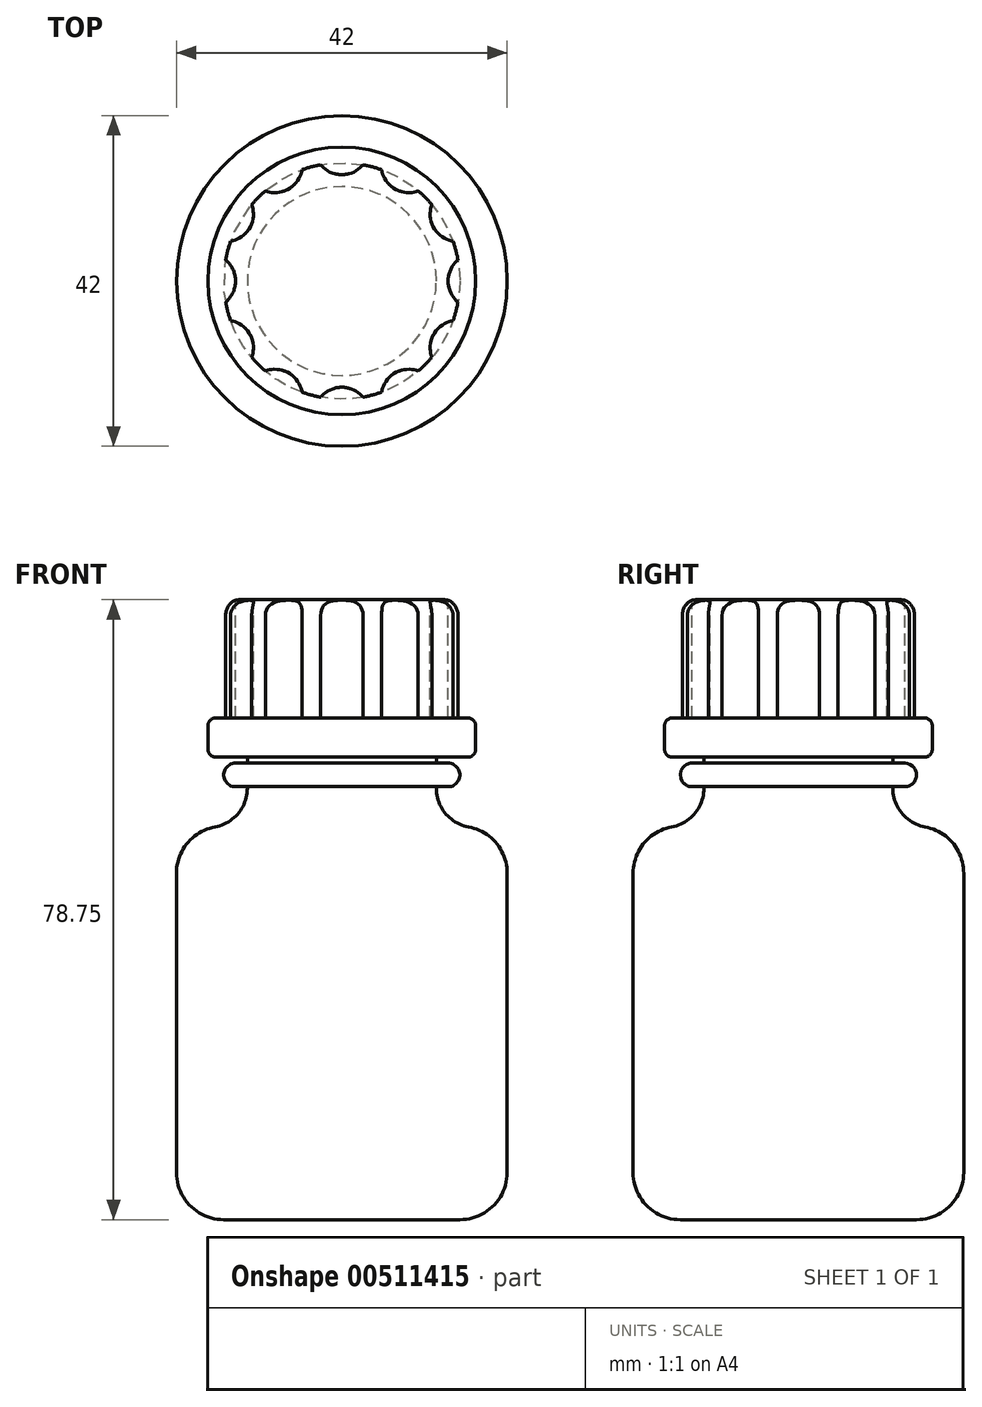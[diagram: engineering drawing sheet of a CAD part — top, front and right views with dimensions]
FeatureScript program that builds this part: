
annotation { "Feature Type Name" : "Feature", "Feature Type Description" : "" }
export const myFeature = defineFeature(function(context is Context, id is Id, definition is map)
    precondition{}
    {
        {
            var Q0;
            Q0=qCreatedBy(makeId("Front.planeOp"),FACE);
            var sketch = newSketch(context, id + "F0", { "sketchPlane" : qUnion([Q0])});
            skLineSegment(sketch, "E0", {"start": v(0, 0) * mm, "end": v(-21, 0) * mm});
            skLineSegment(sketch, "E1", {"start": v(-21, 0) * mm, "end": v(-21, 50) * mm});
            skLineSegment(sketch, "E2", {"start": v(-21, 50) * mm, "end": v(-12, 50) * mm});
            skLineSegment(sketch, "E3", {"start": v(-12, 50) * mm, "end": v(-12, 55) * mm});
            skLineSegment(sketch, "E4", {"start": v(-12, 55) * mm, "end": v(-15, 55) * mm});
            skLineSegment(sketch, "E5", {"start": v(-15, 55) * mm, "end": v(-15, 58) * mm});
            skLineSegment(sketch, "E6", {"start": v(-15, 58) * mm, "end": v(-12, 58) * mm});
            skLineSegment(sketch, "E7", {"start": v(-12, 58) * mm, "end": v(-12, 58.75) * mm});
            skLineSegment(sketch, "E8", {"start": v(-12, 58.75) * mm, "end": v(-17, 58.75) * mm});
            skLineSegment(sketch, "E9", {"start": v(-15, 78.75) * mm, "end": v(0, 78.75) * mm});
            skLineSegment(sketch, "E10", {"start": v(0, 78.75) * mm, "end": v(0, 0) * mm});
            skLineSegment(sketch, "E11", {"start": v(-17, 63.75) * mm, "end": v(-15, 63.75) * mm});
            skLineSegment(sketch, "E12", {"start": v(-15, 63.75) * mm, "end": v(-15, 78.75) * mm});
            skLineSegment(sketch, "E13", {"start": v(-17, 58.75) * mm, "end": v(-17, 63.75) * mm});
            skLineSegment(sketch, "E14", {"start": v(0, 95.38) * mm, "end": v(0, -29.5) * mm, "construction": true});
            skSolve(sketch);
        }
        {
            var Q0;
            Q0 = qSketchRegion(id + "F0", true);
            var Q1;
            Q1=sQuery(id+"F0.wireOp",EDGE,"E14");
            revolve(context, id + "F1", {"entities" : qUnion([Q0]), "axis" : qUnion([Q1]), "revolveType" : RevolveType.FULL});
        }
        {
            var Q0;
            Q0=makeQuery(id+"F1.opRevolve","SWEPT_EDGE",EDGE,{"disambiguationData":[OSD([sQuery(id+"F0.wireOp",EDGE,"E0"),sQuery(id+"F0.wireOp",EDGE,"E1")])]});
            fillet(context, id + "F2", {"entities" : qUnion([Q0]), "radius" : 6 * mm, "tangentPropagation" : true, "allowEdgeOverflow" : false});
        }
        {
            var Q0;
            Q0=makeQuery(id+"F1.opRevolve","SWEPT_EDGE",EDGE,{"disambiguationData":[OSD([sQuery(id+"F0.wireOp",EDGE,"E1"),sQuery(id+"F0.wireOp",EDGE,"E2")])]});
            fillet(context, id + "F3", {"entities" : qUnion([Q0]), "radius" : 6 * mm, "tangentPropagation" : true, "allowEdgeOverflow" : false});
        }
        {
            var Q0;
            Q0=makeQuery(id+"F1.opRevolve","SWEPT_EDGE",EDGE,{"disambiguationData":[OSD([sQuery(id+"F0.wireOp",EDGE,"E2"),sQuery(id+"F0.wireOp",EDGE,"E3")])]});
            fillet(context, id + "F4", {"entities" : qUnion([Q0]), "radius" : 5 * mm, "tangentPropagation" : true, "allowEdgeOverflow" : false});
        }
        {
            var Q0;
            Q0=makeQuery(id+"F1.opRevolve","SWEPT_EDGE",EDGE,{"disambiguationData":[OSD([sQuery(id+"F0.wireOp",EDGE,"E4"),sQuery(id+"F0.wireOp",EDGE,"E5")])]});
            var Q1;
            Q1=makeQuery(id+"F1.opRevolve","SWEPT_EDGE",EDGE,{"disambiguationData":[OSD([sQuery(id+"F0.wireOp",EDGE,"E5"),sQuery(id+"F0.wireOp",EDGE,"E6")])]});
            fillet(context, id + "F5", {"entities" : qUnion([Q0, Q1]), "radius" : 1.5 * mm, "tangentPropagation" : true, "allowEdgeOverflow" : false});
        }
        {
            var Q0;
            Q0=makeQuery(id+"F1.opRevolve","SWEPT_EDGE",EDGE,{"disambiguationData":[OSD([sQuery(id+"F0.wireOp",EDGE,"E8"),sQuery(id+"F0.wireOp",EDGE,"E13")])]});
            var Q1;
            Q1=makeQuery(id+"F1.opRevolve","SWEPT_EDGE",EDGE,{"disambiguationData":[OSD([sQuery(id+"F0.wireOp",EDGE,"E11"),sQuery(id+"F0.wireOp",EDGE,"E13")])]});
            fillet(context, id + "F6", {"entities" : qUnion([Q0, Q1]), "radius" : 1 * mm, "tangentPropagation" : true, "allowEdgeOverflow" : false});
        }
        {
            var Q0;
            Q0=makeQuery(id+"F1.opRevolve","SWEPT_EDGE",EDGE,{"disambiguationData":[OSD([sQuery(id+"F0.wireOp",EDGE,"E9"),sQuery(id+"F0.wireOp",EDGE,"E12")])]});
            fillet(context, id + "F7", {"entities" : qUnion([Q0]), "radius" : 2 * mm, "tangentPropagation" : true, "allowEdgeOverflow" : false});
        }
        {
            var Q0;
            Q0=makeQuery(id+"F1.opRevolve","SWEPT_FACE",FACE,{"disambiguationData":[OSD([sQuery(id+"F0.wireOp",EDGE,"E9")])]});
            var sketch = newSketch(context, id + "F8", { "sketchPlane" : qUnion([Q0])});
            skCircle(sketch, "E15", {"center": v(0, 0) * mm, "radius": 17 * mm, "construction": true});
            skCircle(sketch, "E16", {"center": v(0, 17) * mm, "radius": 3.5 * mm});
            skCircle(sketch, "E17.1.0", {"center": v(-8.5, 14.72) * mm, "radius": 3.5 * mm});
            skCircle(sketch, "E17.2.0", {"center": v(-14.72, 8.5) * mm, "radius": 3.5 * mm});
            skCircle(sketch, "E17.3.0", {"center": v(-17, 0) * mm, "radius": 3.5 * mm});
            skCircle(sketch, "E17.4.0", {"center": v(-14.72, -8.5) * mm, "radius": 3.5 * mm});
            skCircle(sketch, "E17.5.0", {"center": v(-8.5, -14.72) * mm, "radius": 3.5 * mm});
            skCircle(sketch, "E17.6.0", {"center": v(0, -17) * mm, "radius": 3.5 * mm});
            skCircle(sketch, "E17.7.0", {"center": v(8.5, -14.72) * mm, "radius": 3.5 * mm});
            skCircle(sketch, "E17.8.0", {"center": v(14.72, -8.5) * mm, "radius": 3.5 * mm});
            skCircle(sketch, "E17.9.0", {"center": v(17, 0) * mm, "radius": 3.5 * mm});
            skCircle(sketch, "E18.1.10.0", {"center": v(14.72, 8.5) * mm, "radius": 3.5 * mm});
            skCircle(sketch, "E18.1.11.0", {"center": v(8.5, 14.72) * mm, "radius": 3.5 * mm});
            skSolve(sketch);
        }
        {
            var Q0;
            {var subQ0=sQuery(id+"F8.wireOp",EDGE,"E16");var subQ1=sQuery(id+"F0.wireOp",EDGE,"E9");var subQ2=makeQuery(id+"F6.opFillet","BLEND_EDGE",EDGE,{"blendedFrom":[makeQuery(id+"F1.opRevolve","SWEPT_EDGE",EDGE,{"disambiguationData":[OSD([subQ1,sQuery(id+"F0.wireOp",EDGE,"E12")])]}),makeQuery(id+"F1.opRevolve","SWEPT_FACE",FACE,{"disambiguationData":[OSD([subQ1])]})],"blendedInto":[makeQuery(id+"F1.opRevolve","SWEPT_FACE",FACE,{"disambiguationData":[OSD([subQ1])]})]});var subQ3=makeQuery(id+"F8.imprint","INTERSECT",VERTEX,{"disambiguationData":[OD(0.0)],"derivedFrom":[subQ2,subQ0]});Q0=makeQuery(id+"F8.imprint","IMPRINT",FACE,{"disambiguationData":[TD([[makeQuery(id+"F8.imprint","IMPRINT",EDGE,{"disambiguationData":[TD([[subQ3,1.0]])],"derivedFrom":subQ0}),1.0]])]});}
            var Q1;
            Q1 = qSketchRegion(id + "F8", true);
            extrude(context, id + "F9", {"entities" : qUnion([Q0, Q1]), "operationType" : NewBodyOperationType.REMOVE, "oppositeDirection" : true, "depth" : 15 * mm});
        }
    });
